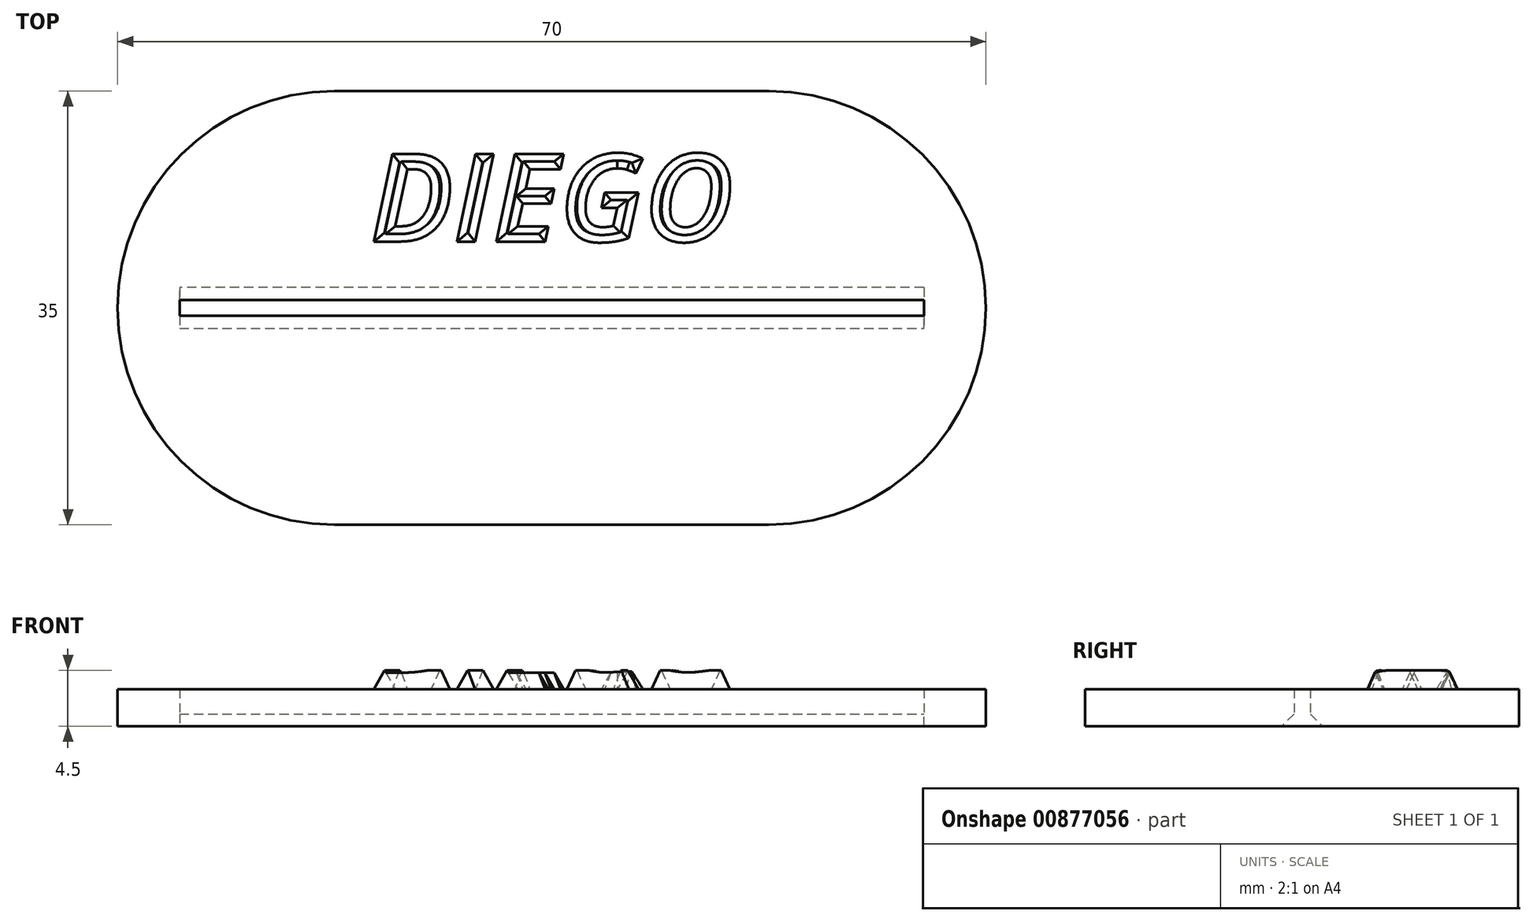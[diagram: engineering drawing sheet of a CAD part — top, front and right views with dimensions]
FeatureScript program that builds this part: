
annotation { "Feature Type Name" : "Feature", "Feature Type Description" : "" }
export const myFeature = defineFeature(function(context is Context, id is Id, definition is map)
    precondition{}
    {
        {
            var Q0;
            Q0=qCreatedBy(makeId("Top.planeOp"),FACE);
            var sketch = newSketch(context, id + "F0", { "sketchPlane" : qUnion([Q0])});
            skLineSegment(sketch, "E0.bottom", {"start": v(0, 0) * mm, "end": v(70, 0) * mm});
            skLineSegment(sketch, "E0.top", {"start": v(0, 35) * mm, "end": v(70, 35) * mm});
            skLineSegment(sketch, "E0.left", {"start": v(0, 0) * mm, "end": v(0, 35) * mm});
            skLineSegment(sketch, "E0.right", {"start": v(70, 0) * mm, "end": v(70, 35) * mm});
            skLineSegment(sketch, "E1.bottom", {"start": v(5, 18.15) * mm, "end": v(65, 18.15) * mm});
            skLineSegment(sketch, "E1.top", {"start": v(5, 16.85) * mm, "end": v(65, 16.85) * mm});
            skLineSegment(sketch, "E1.left", {"start": v(5, 18.15) * mm, "end": v(5, 16.85) * mm});
            skLineSegment(sketch, "E1.right", {"start": v(65, 18.15) * mm, "end": v(65, 16.85) * mm});
            skSolve(sketch);
        }
        {
            var Q0;
            Q0=qSketchRegion(id+"F0",true);
            extrude(context, id + "F1", {"entities" : qUnion([Q0]), "depth" : 3 * mm, "offsetDistance" : 25 * mm});
        }
        {
            var Q0;
            Q0=makeQuery(id+"F1.opExtrude","SWEPT_EDGE",EDGE,{"disambiguationData":[OSD([sQuery(id+"F0.wireOp",EDGE,"E0.bottom"),sQuery(id+"F0.wireOp",EDGE,"E0.right")])]});
            var Q1;
            Q1=makeQuery(id+"F1.opExtrude","SWEPT_EDGE",EDGE,{"disambiguationData":[OSD([sQuery(id+"F0.wireOp",EDGE,"E0.top"),sQuery(id+"F0.wireOp",EDGE,"E0.right")])]});
            var Q2;
            Q2=makeQuery(id+"F1.opExtrude","SWEPT_EDGE",EDGE,{"disambiguationData":[OSD([sQuery(id+"F0.wireOp",EDGE,"E0.top"),sQuery(id+"F0.wireOp",EDGE,"E0.left")])]});
            var Q3;
            Q3=makeQuery(id+"F1.opExtrude","SWEPT_EDGE",EDGE,{"disambiguationData":[OSD([sQuery(id+"F0.wireOp",EDGE,"E0.bottom"),sQuery(id+"F0.wireOp",EDGE,"E0.left")])]});
            fillet(context, id + "F2", {"entities" : qUnion([Q0, Q1, Q2, Q3]), "radius" : 17.5 * mm, "tangentPropagation" : true, "allowEdgeOverflow" : false});
        }
        {
            var Q0;
            Q0=makeQuery(id+"F1.opExtrude","CAP_EDGE",EDGE,{"disambiguationData":[OSD([sQuery(id+"F0.wireOp",EDGE,"E1.top")])],"isStart":true});
            var Q1;
            Q1=makeQuery(id+"F1.opExtrude","CAP_EDGE",EDGE,{"disambiguationData":[OSD([sQuery(id+"F0.wireOp",EDGE,"E1.bottom")])],"isStart":true});
            chamfer(context, id + "F3", {"entities" : qUnion([Q0, Q1]), "width" : 1 * mm, "tangentPropagation" : true});
        }
        {
            var Q0;
            Q0=makeQuery(id+"F1.opExtrude","CAP_FACE",FACE,{"disambiguationData":[OSD([sQuery(id+"F0.wireOp",EDGE,"E0.bottom"),sQuery(id+"F0.wireOp",EDGE,"E0.top"),sQuery(id+"F0.wireOp",EDGE,"E0.left"),sQuery(id+"F0.wireOp",EDGE,"E0.right"),sQuery(id+"F0.wireOp",EDGE,"E1.bottom"),sQuery(id+"F0.wireOp",EDGE,"E1.top"),sQuery(id+"F0.wireOp",EDGE,"E1.left"),sQuery(id+"F0.wireOp",EDGE,"E1.right")])],"isStart":false});
            var sketch = newSketch(context, id + "F4", { "sketchPlane" : qUnion([Q0])});
            skText(sketch, "E2", { "text": "DIEGO", "fontName": "OpenSans-BoldItalic.ttf"});
            const initialGuessF4  = {"E2": [0.0204, 0.02285, 1, 0, 0.00712]};
            skSetInitialGuess(sketch, initialGuessF4);
            skSolve(sketch);
        }
        {
            var Q0;
            Q0=qSketchRegion(id+"F4",true);
            extrude(context, id + "F5", {"entities" : qUnion([Q0]), "depth" : 1.5 * mm, "offsetDistance" : 25 * mm, "hasDraft" : true, "draftAngle" : 25 * degree, "draftPullDirection" : true});
        }
    });
